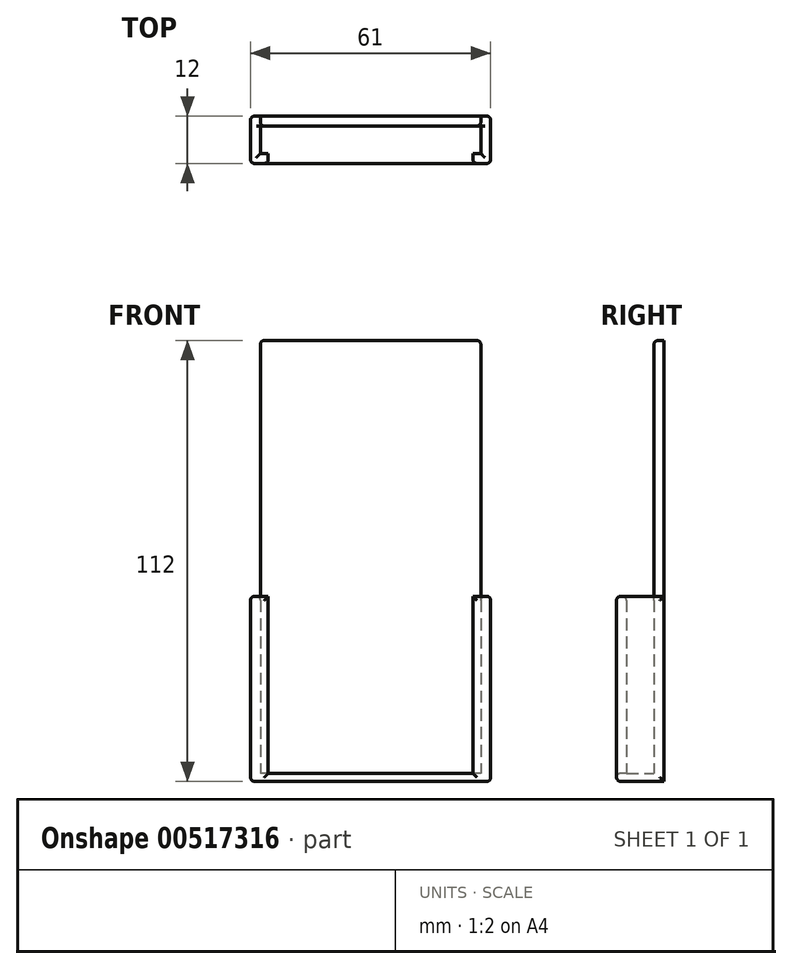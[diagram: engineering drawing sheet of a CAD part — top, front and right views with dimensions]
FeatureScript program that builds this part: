
annotation { "Feature Type Name" : "Feature", "Feature Type Description" : "" }
export const myFeature = defineFeature(function(context is Context, id is Id, definition is map)
    precondition{}
    {
        {
            var Q0;
            Q0=qCreatedBy(makeId("Top.planeOp"),FACE);
            var sketch = newSketch(context, id + "F0", { "sketchPlane" : qUnion([Q0])});
            skLineSegment(sketch, "E0.bottom", {"start": v(28, -3.5) * mm, "end": v(-28, -3.5) * mm});
            skLineSegment(sketch, "E0.top", {"start": v(28, 3.5) * mm, "end": v(-28, 3.5) * mm});
            skLineSegment(sketch, "E0.left", {"start": v(28, -3.5) * mm, "end": v(28, 3.5) * mm});
            skLineSegment(sketch, "E0.right", {"start": v(-28, -3.5) * mm, "end": v(-28, 3.5) * mm});
            skPoint(sketch, "E0.middle", {"position": v(0, 0) * mm});
            skLineSegment(sketch, "E1.0", {"start": v(30.5, -6) * mm, "end": v(-30.5, -6) * mm});
            skLineSegment(sketch, "E1.1", {"start": v(30.5, -6) * mm, "end": v(30.5, 6) * mm});
            skLineSegment(sketch, "E1.2", {"start": v(30.5, 6) * mm, "end": v(-30.5, 6) * mm});
            skLineSegment(sketch, "E1.3", {"start": v(-30.5, -6) * mm, "end": v(-30.5, 6) * mm});
            skSolve(sketch);
        }
        {
            var Q0;
            Q0 = qSketchRegion(id + "F0", true);
            extrude(context, id + "F1", {"entities" : qUnion([Q0]), "depth" : 45 * mm, "offsetDistance" : 25 * mm});
        }
        {
            var Q0;
            Q0=makeQuery(id+"F1.opExtrude","SWEPT_FACE",FACE,{"disambiguationData":[OSD([sQuery(id+"F0.wireOp",EDGE,"E1.0")])]});
            var sketch = newSketch(context, id + "F2", { "sketchPlane" : qUnion([Q0])});
            skLineSegment(sketch, "E2.bottom", {"start": v(-26, 45) * mm, "end": v(26, 45) * mm});
            skLineSegment(sketch, "E2.top", {"start": v(-26, 0) * mm, "end": v(26, 0) * mm});
            skLineSegment(sketch, "E2.left", {"start": v(-26, 45) * mm, "end": v(-26, 0) * mm});
            skLineSegment(sketch, "E2.right", {"start": v(26, 45) * mm, "end": v(26, 0) * mm});
            skSolve(sketch);
        }
        {
            var Q0;
            Q0 = qSketchRegion(id + "F2", true);
            extrude(context, id + "F3", {"entities" : qUnion([Q0]), "operationType" : NewBodyOperationType.REMOVE, "oppositeDirection" : true, "depth" : 3 * mm, "offsetDistance" : 25 * mm});
        }
        {
            var Q0;
            Q0=makeQuery(id+"F1.opExtrude","CAP_FACE",FACE,{"disambiguationData":[OSD([sQuery(id+"F0.wireOp",EDGE,"E0.bottom"),sQuery(id+"F0.wireOp",EDGE,"E0.top"),sQuery(id+"F0.wireOp",EDGE,"E0.left"),sQuery(id+"F0.wireOp",EDGE,"E0.right"),sQuery(id+"F0.wireOp",EDGE,"E1.0"),sQuery(id+"F0.wireOp",EDGE,"E1.1"),sQuery(id+"F0.wireOp",EDGE,"E1.2"),sQuery(id+"F0.wireOp",EDGE,"E1.3")])],"isStart":true});
            var sketch = newSketch(context, id + "F4", { "sketchPlane" : qUnion([Q0])});
            skLineSegment(sketch, "E3.bottom", {"start": v(-30.5, -6) * mm, "end": v(30.5, -6) * mm});
            skLineSegment(sketch, "E3.top", {"start": v(-30.5, 6) * mm, "end": v(30.5, 6) * mm});
            skLineSegment(sketch, "E3.left", {"start": v(-30.5, -6) * mm, "end": v(-30.5, 6) * mm});
            skLineSegment(sketch, "E3.right", {"start": v(30.5, -6) * mm, "end": v(30.5, 6) * mm});
            skSolve(sketch);
        }
        {
            var Q0;
            Q0 = qSketchRegion(id + "F4", true);
            extrude(context, id + "F5", {"entities" : qUnion([Q0]), "operationType" : NewBodyOperationType.ADD, "depth" : 2 * mm, "offsetDistance" : 25 * mm});
        }
        {
            var Q0;
            Q0=makeQuery(id+"F1.opExtrude","CAP_FACE",FACE,{"disambiguationData":[OSD([sQuery(id+"F0.wireOp",EDGE,"E0.bottom"),sQuery(id+"F0.wireOp",EDGE,"E0.top"),sQuery(id+"F0.wireOp",EDGE,"E0.left"),sQuery(id+"F0.wireOp",EDGE,"E0.right"),sQuery(id+"F0.wireOp",EDGE,"E1.0"),sQuery(id+"F0.wireOp",EDGE,"E1.1"),sQuery(id+"F0.wireOp",EDGE,"E1.2"),sQuery(id+"F0.wireOp",EDGE,"E1.3")])],"isStart":false});
            var sketch = newSketch(context, id + "F6", { "sketchPlane" : qUnion([Q0])});
            skLineSegment(sketch, "E4.bottom", {"start": v(28, 3.5) * mm, "end": v(-28, 3.5) * mm});
            skLineSegment(sketch, "E4.top", {"start": v(28, 6) * mm, "end": v(-28, 6) * mm});
            skLineSegment(sketch, "E4.left", {"start": v(28, 3.5) * mm, "end": v(28, 6) * mm});
            skLineSegment(sketch, "E4.right", {"start": v(-28, 3.5) * mm, "end": v(-28, 6) * mm});
            skSolve(sketch);
        }
        {
            var Q0;
            Q0 = qSketchRegion(id + "F6", true);
            extrude(context, id + "F7", {"entities" : qUnion([Q0]), "operationType" : NewBodyOperationType.ADD, "depth" : 65 * mm, "offsetDistance" : 25 * mm});
        }
        {
            var Q0;
            {var subQ0=sQuery(id+"F0.wireOp",EDGE,"E1.3");var subQ2=sQuery(id+"F0.wireOp",EDGE,"E1.1");var subQ3=sQuery(id+"F0.wireOp",EDGE,"E1.0");var subQ10=makeQuery(id+"F1.opExtrude","SWEPT_FACE",FACE,{"disambiguationData":[OSD([subQ3])]});Q0=makeQuery(id+"F5.boolean.opBoolean","MERGE",FACE,{"derivedFrom":[makeQuery(id+"F3.boolean.opBoolean","SPLIT",FACE,{"disambiguationData":[TD([makeQuery(id+"F1.opExtrude","SWEPT_FACE",FACE,{"disambiguationData":[OSD([subQ2])]})])],"derivedFrom":subQ10}),makeQuery(id+"F3.boolean.opBoolean","SPLIT",FACE,{"disambiguationData":[TD([makeQuery(id+"F1.opExtrude","SWEPT_FACE",FACE,{"disambiguationData":[OSD([subQ0])]})])],"derivedFrom":subQ10}),makeQuery(id+"F5.opExtrude","SWEPT_FACE",FACE,{"disambiguationData":[OSD([sQuery(id+"F4.wireOp",EDGE,"E3.top")])]})]});}
            var Q1;
            Q1=makeQuery(id+"F1.opExtrude","CAP_EDGE",EDGE,{"disambiguationData":[OSD([sQuery(id+"F0.wireOp",EDGE,"E0.right")])],"isStart":false});
            var Q2;
            Q2=makeQuery(id+"F1.opExtrude","CAP_EDGE",EDGE,{"disambiguationData":[OSD([sQuery(id+"F0.wireOp",EDGE,"E0.left")])],"isStart":false});
            var Q3;
            {var subQ0=sQuery(id+"F0.wireOp",EDGE,"E0.bottom");var subQ1=sQuery(id+"F0.wireOp",EDGE,"E0.left");Q3=makeQuery(id+"F3.boolean.opBoolean","SPLIT",EDGE,{"disambiguationData":[TD([makeQuery(id+"F1.opExtrude","SWEPT_FACE",FACE,{"disambiguationData":[OSD([subQ1])]})])],"derivedFrom":makeQuery(id+"F1.opExtrude","CAP_EDGE",EDGE,{"disambiguationData":[OSD([subQ0])],"isStart":false})});}
            var Q4;
            {var subQ0=sQuery(id+"F0.wireOp",EDGE,"E0.bottom");var subQ1=sQuery(id+"F0.wireOp",EDGE,"E0.right");Q4=makeQuery(id+"F3.boolean.opBoolean","SPLIT",EDGE,{"disambiguationData":[TD([makeQuery(id+"F1.opExtrude","SWEPT_FACE",FACE,{"disambiguationData":[OSD([subQ1])]})])],"derivedFrom":makeQuery(id+"F1.opExtrude","CAP_EDGE",EDGE,{"disambiguationData":[OSD([subQ0])],"isStart":false})});}
            var Q5;
            Q5=makeQuery(id+"F1.opExtrude","CAP_EDGE",EDGE,{"disambiguationData":[OSD([sQuery(id+"F0.wireOp",EDGE,"E1.3")])],"isStart":false});
            var Q6;
            Q6=makeQuery(id+"F1.opExtrude","CAP_EDGE",EDGE,{"disambiguationData":[OSD([sQuery(id+"F0.wireOp",EDGE,"E1.1")])],"isStart":false});
            var Q7;
            Q7=makeQuery(id+"F5.boolean.opBoolean","MERGE",FACE,{"derivedFrom":[makeQuery(id+"F1.opExtrude","SWEPT_FACE",FACE,{"disambiguationData":[OSD([sQuery(id+"F0.wireOp",EDGE,"E1.1")])]}),makeQuery(id+"F5.opExtrude","SWEPT_FACE",FACE,{"disambiguationData":[OSD([sQuery(id+"F4.wireOp",EDGE,"E3.right")])]})]});
            var Q8;
            Q8=makeQuery(id+"F5.boolean.opBoolean","MERGE",FACE,{"derivedFrom":[makeQuery(id+"F1.opExtrude","SWEPT_FACE",FACE,{"disambiguationData":[OSD([sQuery(id+"F0.wireOp",EDGE,"E1.3")])]}),makeQuery(id+"F5.opExtrude","SWEPT_FACE",FACE,{"disambiguationData":[OSD([sQuery(id+"F4.wireOp",EDGE,"E3.left")])]})]});
            var Q9;
            Q9=makeQuery(id+"F7.opExtrude","CAP_EDGE",EDGE,{"disambiguationData":[OSD([sQuery(id+"F6.wireOp",EDGE,"E4.bottom")])],"isStart":false});
            fillet(context, id + "F8", {"entities" : qUnion([Q0, Q1, Q2, Q3, Q4, Q5, Q6, Q7, Q8, Q9]), "radius" : 1 * mm, "tangentPropagation" : true, "allowEdgeOverflow" : false});
        }
        {
            var Q0;
            Q0=makeQuery(id+"F7.opExtrude","SWEPT_EDGE",EDGE,{"disambiguationData":[OSD([sQuery(id+"F0.wireOp",EDGE,"E0.right"),sQuery(id+"F6.wireOp",EDGE,"E4.bottom"),sQuery(id+"F6.wireOp",EDGE,"E4.right")])]});
            var Q1;
            Q1=makeQuery(id+"F7.opExtrude","SWEPT_EDGE",EDGE,{"disambiguationData":[OSD([sQuery(id+"F0.wireOp",EDGE,"E0.left"),sQuery(id+"F6.wireOp",EDGE,"E4.bottom"),sQuery(id+"F6.wireOp",EDGE,"E4.left")])]});
            fillet(context, id + "F9", {"entities" : qUnion([Q0, Q1]), "radius" : 1 * mm, "tangentPropagation" : true, "allowEdgeOverflow" : false});
        }
    });
